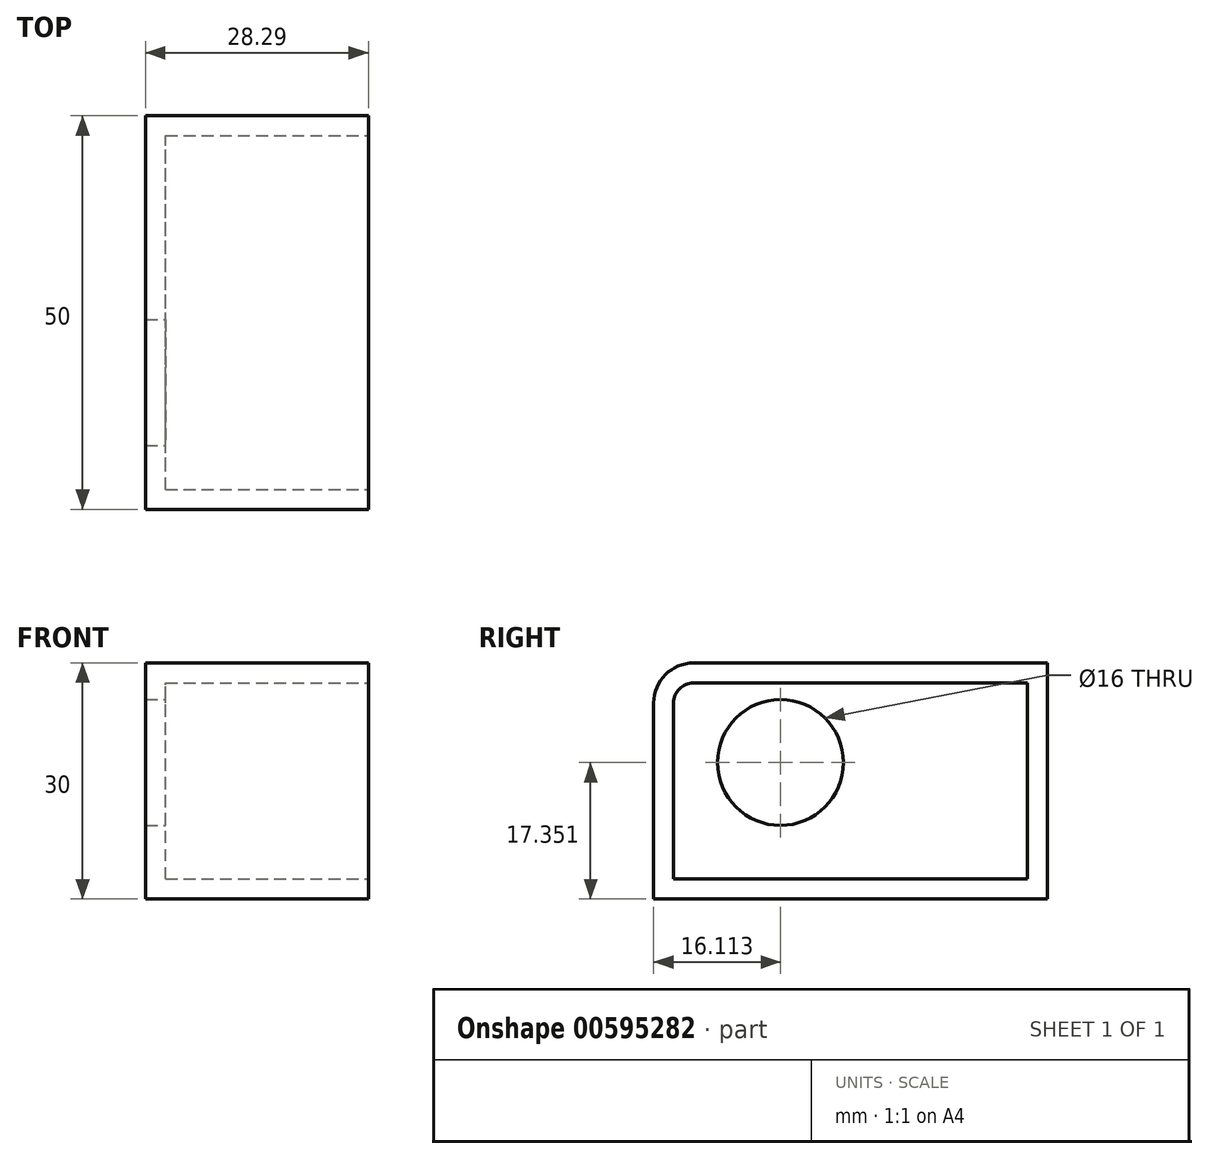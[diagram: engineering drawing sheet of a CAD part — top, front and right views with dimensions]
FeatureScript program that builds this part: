
annotation { "Feature Type Name" : "Feature", "Feature Type Description" : "" }
export const myFeature = defineFeature(function(context is Context, id is Id, definition is map)
    precondition{}
    {
        {
            var Q0;
            Q0=qCreatedBy(makeId("Front.planeOp"),FACE);
            var sketch = newSketch(context, id + "F0", { "sketchPlane" : qUnion([Q0])});
            skLineSegment(sketch, "E0.bottom", {"start": v(6.74, 4.07) * mm, "end": v(35.03, 4.07) * mm});
            skLineSegment(sketch, "E0.top", {"start": v(6.74, 34.07) * mm, "end": v(35.03, 34.07) * mm});
            skLineSegment(sketch, "E0.left", {"start": v(6.74, 4.07) * mm, "end": v(6.74, 34.07) * mm});
            skLineSegment(sketch, "E0.right", {"start": v(35.03, 4.07) * mm, "end": v(35.03, 34.07) * mm});
            skSolve(sketch);
        }
        {
            var Q0;
            Q0 = qSketchRegion(id + "F0", true);
            extrude(context, id + "F1", {"entities" : qUnion([Q0]), "depth" : 50 * mm, "offsetDistance" : 25.4 * mm});
        }
        {
            var Q0;
            Q0=makeQuery(id+"F1.opExtrude","CAP_EDGE",EDGE,{"disambiguationData":[OSD([sQuery(id+"F0.wireOp",EDGE,"E0.top")])],"isStart":false});
            fillet(context, id + "F2", {"entities" : qUnion([Q0]), "radius" : 5.08 * mm, "tangentPropagation" : true, "allowEdgeOverflow" : false});
        }
        {
            var Q0;
            Q0=makeQuery(id+"F1.opExtrude","SWEPT_FACE",FACE,{"disambiguationData":[OSD([sQuery(id+"F0.wireOp",EDGE,"E0.right")])]});
            shell(context, id + "F3", {"entities" : qUnion([Q0]), "thickness" : 2.54 * mm});
        }
        {
            var Q0;
            Q0=makeQuery(id+"F3.opShell","OFFSET_FACE",FACE,{"disambiguationData":[OSD([sQuery(id+"F0.wireOp",EDGE,"E0.left")])]});
            var sketch = newSketch(context, id + "F4", { "sketchPlane" : qUnion([Q0])});
            skCircle(sketch, "E1", {"center": v(-33.89, 21.42) * mm, "radius": 8 * mm});
            skSolve(sketch);
        }
        {
            var Q0;
            Q0=makeQuery(id+"F4.imprint","IMPRINT",FACE,{"disambiguationData":[TD([[makeQuery(id+"F4.imprint","IMPRINT",EDGE,{"derivedFrom":sQuery(id+"F4.wireOp",EDGE,"E1")}),1.0]])]});
            extrude(context, id + "F5", {"entities" : qUnion([Q0]), "operationType" : NewBodyOperationType.REMOVE, "oppositeDirection" : true, "depth" : 9.1 * mm, "offsetDistance" : 25 * mm});
        }
    });
